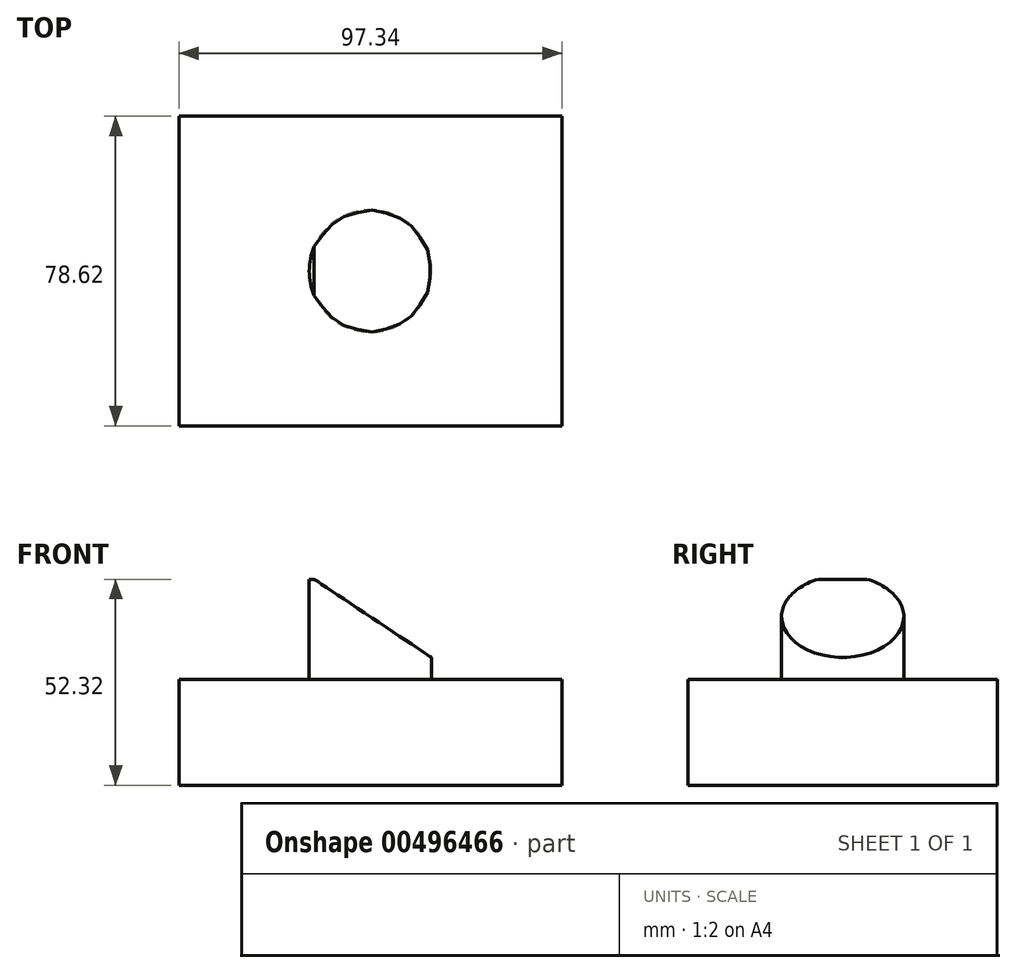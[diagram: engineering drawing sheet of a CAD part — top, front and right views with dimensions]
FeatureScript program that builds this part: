
annotation { "Feature Type Name" : "Feature", "Feature Type Description" : "" }
export const myFeature = defineFeature(function(context is Context, id is Id, definition is map)
    precondition{}
    {
        {
            var Q0;
            Q0=qCreatedBy(makeId("Top.planeOp"),FACE);
            var sketch = newSketch(context, id + "F0", { "sketchPlane" : qUnion([Q0])});
            skLineSegment(sketch, "E0.bottom", {"start": v(-48.67, 39.31) * mm, "end": v(48.67, 39.31) * mm});
            skLineSegment(sketch, "E0.top", {"start": v(-48.67, -39.31) * mm, "end": v(48.67, -39.31) * mm});
            skLineSegment(sketch, "E0.left", {"start": v(-48.67, 39.31) * mm, "end": v(-48.67, -39.31) * mm});
            skLineSegment(sketch, "E0.right", {"start": v(48.67, 39.31) * mm, "end": v(48.67, -39.31) * mm});
            skPoint(sketch, "E0.middle", {"position": v(0, 0) * mm});
            skSolve(sketch);
        }
        {
            var Q0;
            Q0=makeQuery(id+"F0.imprint","IMPRINT",FACE,{"disambiguationData":[TD([[makeQuery(id+"F0.imprint","IMPRINT",EDGE,{"derivedFrom":sQuery(id+"F0.wireOp",EDGE,"E0.bottom")}),-1.0]])]});
            extrude(context, id + "F1", {"entities" : qUnion([Q0]), "oppositeDirection" : true, "depth" : 26.92 * mm});
        }
        {
            var Q0;
            Q0=qCreatedBy(makeId("Top.planeOp"),FACE);
            var sketch = newSketch(context, id + "F2", { "sketchPlane" : qUnion([Q0])});
            skCircle(sketch, "E1", {"center": v(0, 0) * mm, "radius": 15.54 * mm});
            skSolve(sketch);
        }
        {
            var Q0;
            Q0=makeQuery(id+"F2.imprint","IMPRINT",FACE,{"disambiguationData":[TD([[makeQuery(id+"F2.imprint","IMPRINT",EDGE,{"derivedFrom":sQuery(id+"F2.wireOp",EDGE,"E1")}),1.0]])]});
            extrude(context, id + "F3", {"entities" : qUnion([Q0]), "operationType" : NewBodyOperationType.ADD, "depth" : 25.4 * mm});
        }
        {
            var Q0;
            Q0=qCreatedBy(makeId("Front.planeOp"),FACE);
            var sketch = newSketch(context, id + "F4", { "sketchPlane" : qUnion([Q0])});
            skLineSegment(sketch, "E2", {"start": v(-18.9, 28.5) * mm, "end": v(23.77, 0) * mm});
            skLineSegment(sketch, "E3", {"start": v(23.77, 0) * mm, "end": v(23.77, 28.8) * mm});
            skLineSegment(sketch, "E4", {"start": v(23.77, 28.8) * mm, "end": v(-18.9, 28.5) * mm});
            skSolve(sketch);
        }
        {
            var Q0;
            Q0=makeQuery(id+"F4.imprint","IMPRINT",FACE,{"disambiguationData":[TD([[makeQuery(id+"F4.imprint","IMPRINT",EDGE,{"derivedFrom":sQuery(id+"F4.wireOp",EDGE,"E2")}),1.0]])]});
            extrude(context, id + "F5", {"entities" : qUnion([Q0]), "operationType" : NewBodyOperationType.REMOVE, "endBound" : BoundingType.SYMMETRIC, "depth" : 127 * mm});
        }
    });
